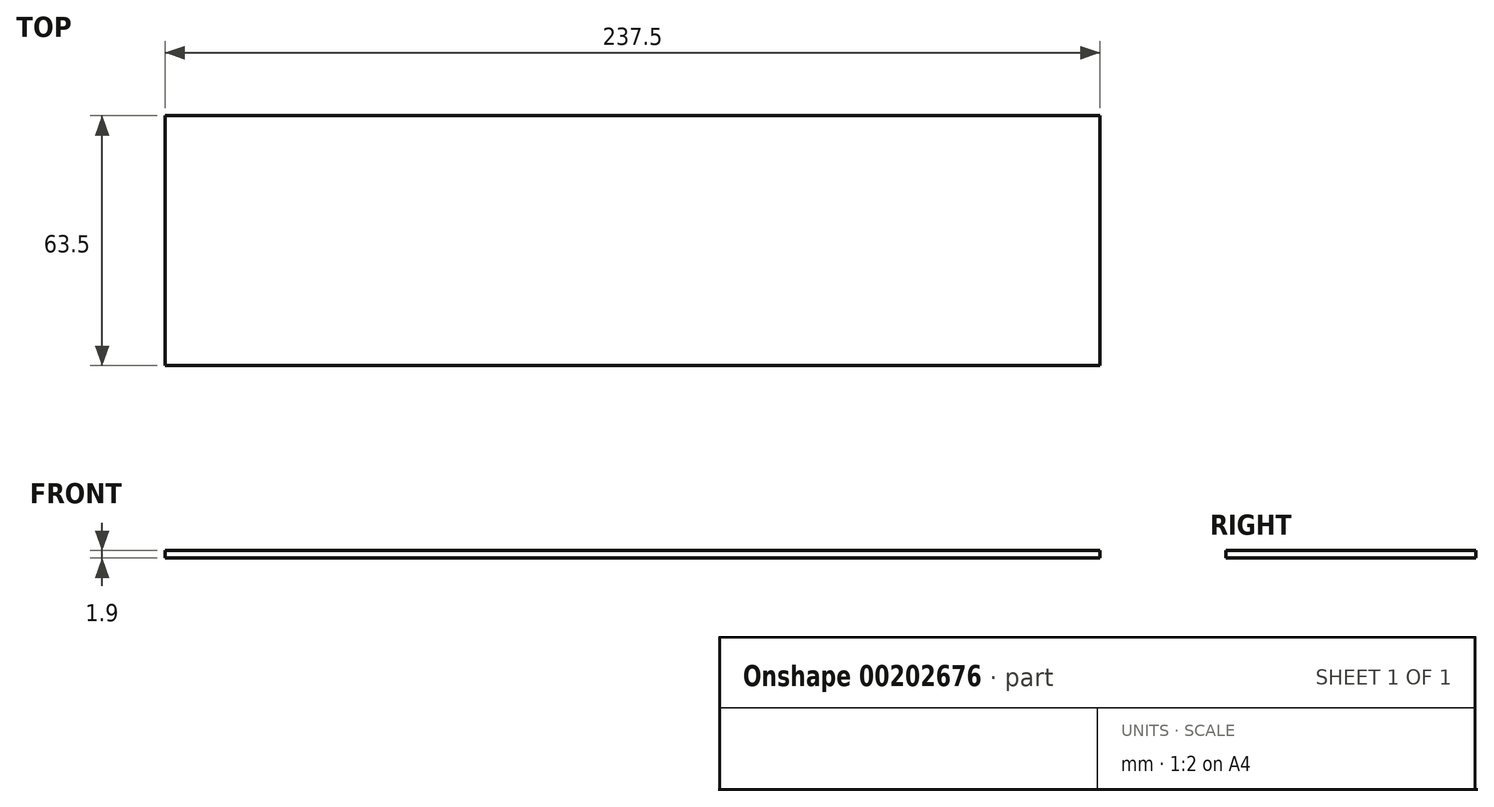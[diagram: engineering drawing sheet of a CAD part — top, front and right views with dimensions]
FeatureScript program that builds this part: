
annotation { "Feature Type Name" : "Feature", "Feature Type Description" : "" }
export const myFeature = defineFeature(function(context is Context, id is Id, definition is map)
    precondition{}
    {
        {
            var Q0;
            Q0=qCreatedBy(makeId("Top.planeOp"),FACE);
            var sketch = newSketch(context, id + "F0", { "sketchPlane" : qUnion([Q0])});
            skLineSegment(sketch, "E0.bottom", {"start": v(-118.75, -31.75) * mm, "end": v(118.75, -31.75) * mm});
            skLineSegment(sketch, "E0.top", {"start": v(-118.75, 31.75) * mm, "end": v(118.75, 31.75) * mm});
            skLineSegment(sketch, "E0.left", {"start": v(-118.75, -31.75) * mm, "end": v(-118.75, 31.75) * mm});
            skLineSegment(sketch, "E0.right", {"start": v(118.75, -31.75) * mm, "end": v(118.75, 31.75) * mm});
            skPoint(sketch, "E0.middle", {"position": v(0, 0) * mm});
            skSolve(sketch);
        }
        {
            var Q0;
            Q0 = qSketchRegion(id + "F0", true);
            extrude(context, id + "F1", {"entities" : qUnion([Q0]), "depth" : 1.9 * mm});
        }
    });
